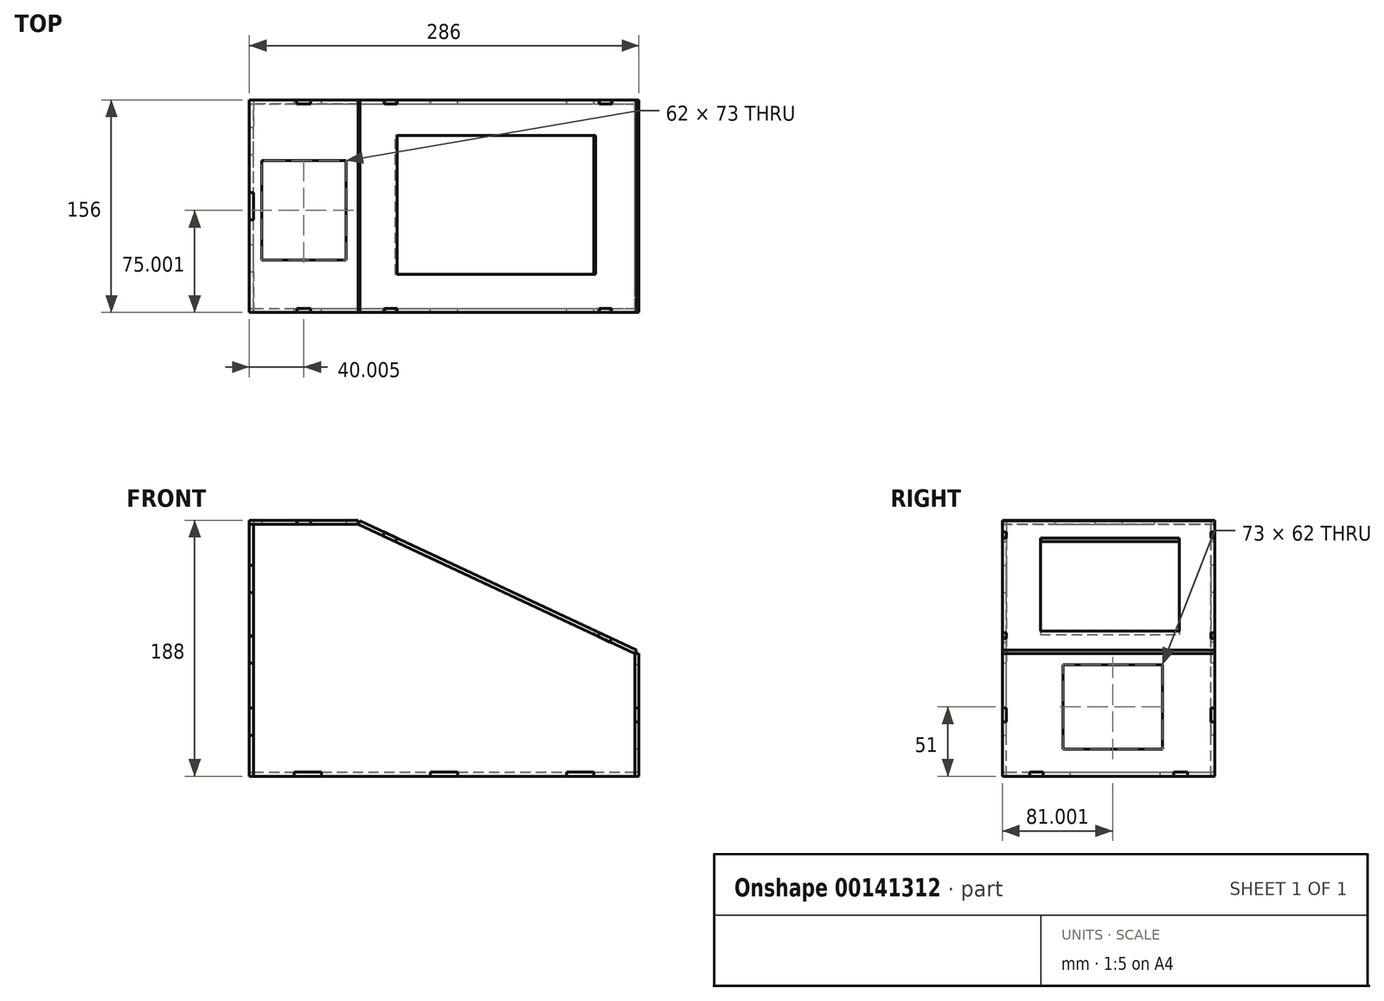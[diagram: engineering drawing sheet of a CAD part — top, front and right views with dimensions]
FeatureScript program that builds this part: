
annotation { "Feature Type Name" : "Feature", "Feature Type Description" : "" }
export const myFeature = defineFeature(function(context is Context, id is Id, definition is map)
    precondition{}
    {
        {
            var Q0;
            Q0=qCreatedBy(makeId("Top.planeOp"),FACE);
            var sketch = newSketch(context, id + "F0", { "sketchPlane" : qUnion([Q0])});
            skLineSegment(sketch, "E0.bottom", {"start": v(-139.67, -69.24) * mm, "end": v(140.33, -69.24) * mm});
            skLineSegment(sketch, "E0.top", {"start": v(-139.67, 80.76) * mm, "end": v(140.33, 80.76) * mm});
            skLineSegment(sketch, "E0.left", {"start": v(-139.67, -69.24) * mm, "end": v(-139.67, 80.76) * mm});
            skLineSegment(sketch, "E0.right", {"start": v(140.33, -69.24) * mm, "end": v(140.33, 80.76) * mm});
            skSolve(sketch);
        }
        {
            var Q0;
            Q0=makeQuery(id+"F0.imprint","IMPRINT",FACE,{"disambiguationData":[TD([[makeQuery(id+"F0.imprint","IMPRINT",EDGE,{"derivedFrom":sQuery(id+"F0.wireOp",EDGE,"E0.bottom")}),1.0]])]});
            extrude(context, id + "F1", {"entities" : qUnion([Q0]), "depth" : 3 * mm});
        }
        {
            var Q0;
            Q0=makeQuery(id+"F1.opExtrude","SWEPT_FACE",FACE,{"disambiguationData":[OSD([sQuery(id+"F0.wireOp",EDGE,"E0.right")])]});
            var sketch = newSketch(context, id + "F2", { "sketchPlane" : qUnion([Q0])});
            skLineSegment(sketch, "E1.bottom", {"start": v(-72.24, 0) * mm, "end": v(83.76, 0) * mm});
            skLineSegment(sketch, "E1.top", {"start": v(-72.24, 90) * mm, "end": v(83.76, 90) * mm});
            skLineSegment(sketch, "E1.left", {"start": v(-72.24, 0) * mm, "end": v(-72.24, 90) * mm});
            skLineSegment(sketch, "E1.right", {"start": v(83.76, 0) * mm, "end": v(83.76, 90) * mm});
            skLineSegment(sketch, "E2.bottom", {"start": v(-27.74, 82) * mm, "end": v(45.26, 82) * mm});
            skLineSegment(sketch, "E2.top", {"start": v(-27.74, 20) * mm, "end": v(45.26, 20) * mm});
            skLineSegment(sketch, "E2.left", {"start": v(-27.74, 82) * mm, "end": v(-27.74, 20) * mm});
            skLineSegment(sketch, "E2.right", {"start": v(45.26, 82) * mm, "end": v(45.26, 20) * mm});
            skLineSegment(sketch, "E3.bottom", {"start": v(-72.24, 50) * mm, "end": v(-69.24, 50) * mm});
            skLineSegment(sketch, "E3.top", {"start": v(-72.24, 40) * mm, "end": v(-69.24, 40) * mm});
            skLineSegment(sketch, "E3.left", {"start": v(-72.24, 50) * mm, "end": v(-72.24, 40) * mm});
            skLineSegment(sketch, "E3.right", {"start": v(-69.24, 50) * mm, "end": v(-69.24, 40) * mm});
            skLineSegment(sketch, "E4.bottom", {"start": v(83.76, 50) * mm, "end": v(80.76, 50) * mm});
            skLineSegment(sketch, "E4.top", {"start": v(83.76, 40) * mm, "end": v(80.76, 40) * mm});
            skLineSegment(sketch, "E4.left", {"start": v(83.76, 50) * mm, "end": v(83.76, 40) * mm});
            skLineSegment(sketch, "E4.right", {"start": v(80.76, 50) * mm, "end": v(80.76, 40) * mm});
            skLineSegment(sketch, "E5.bottom", {"start": v(-52.24, 0) * mm, "end": v(-42.24, 0) * mm});
            skLineSegment(sketch, "E5.top", {"start": v(-52.24, 3) * mm, "end": v(-42.24, 3) * mm});
            skLineSegment(sketch, "E5.left", {"start": v(-52.24, 0) * mm, "end": v(-52.24, 3) * mm});
            skLineSegment(sketch, "E5.right", {"start": v(-42.24, 0) * mm, "end": v(-42.24, 3) * mm});
            skLineSegment(sketch, "E6.bottom", {"start": v(63.76, 0) * mm, "end": v(53.76, 0) * mm});
            skLineSegment(sketch, "E6.top", {"start": v(63.76, 3) * mm, "end": v(53.76, 3) * mm});
            skLineSegment(sketch, "E6.left", {"start": v(63.76, 0) * mm, "end": v(63.76, 3) * mm});
            skLineSegment(sketch, "E6.right", {"start": v(53.76, 0) * mm, "end": v(53.76, 3) * mm});
            skSolve(sketch);
        }
        {
            var Q0;
            Q0=makeQuery(id+"F2.imprint","IMPRINT",FACE,{"disambiguationData":[TD([[makeQuery(id+"F2.imprint","IMPRINT",EDGE,{"derivedFrom":sQuery(id+"F2.wireOp",EDGE,"E1.top")}),-1.0]])]});
            var Q1;
            {var subQ1=sQuery(id+"F0.wireOp",EDGE,"E0.right");Q1=makeQuery(id+"F2.imprint","IMPRINT",FACE,{"disambiguationData":[TD([[makeQuery(id+"F2.imprint","IMPRINT",EDGE,{"derivedFrom":makeQuery(id+"F1.opExtrude","CAP_EDGE",EDGE,{"disambiguationData":[OSD([subQ1])],"isStart":false})}),-1.0]])]});}
            extrude(context, id + "F3", {"entities" : qUnion([Q0, Q1]), "depth" : 3 * mm});
        }
        {
            var Q0;
            Q0=makeQuery(id+"F1.opExtrude","SWEPT_FACE",FACE,{"disambiguationData":[OSD([sQuery(id+"F0.wireOp",EDGE,"E0.left")])]});
            var sketch = newSketch(context, id + "F4", { "sketchPlane" : qUnion([Q0])});
            skLineSegment(sketch, "E7.bottom", {"start": v(-83.76, 0) * mm, "end": v(72.24, 0) * mm});
            skLineSegment(sketch, "E7.top", {"start": v(-83.76, 185) * mm, "end": v(-15.76, 185) * mm});
            skLineSegment(sketch, "E7.left", {"start": v(-83.76, 0) * mm, "end": v(-83.76, 30) * mm});
            skLineSegment(sketch, "E7.right", {"start": v(72.24, 0) * mm, "end": v(72.24, 30) * mm});
            skLineSegment(sketch, "E8.bottom", {"start": v(72.24, 155) * mm, "end": v(69.24, 155) * mm});
            skLineSegment(sketch, "E8.top", {"start": v(72.24, 135) * mm, "end": v(69.24, 135) * mm});
            skLineSegment(sketch, "E8.right", {"start": v(69.24, 155) * mm, "end": v(69.24, 135) * mm});
            skPoint(sketch, "E9.oppositeSnap0", {"position": v(70.74, 135) * mm});
            skLineSegment(sketch, "E9.bottom", {"start": v(-83.76, 155) * mm, "end": v(-80.76, 155) * mm});
            skLineSegment(sketch, "E9.top", {"start": v(-83.76, 135) * mm, "end": v(-80.76, 135) * mm});
            skLineSegment(sketch, "E9.right", {"start": v(-80.76, 155) * mm, "end": v(-80.76, 135) * mm});
            skLineSegment(sketch, "E10.bottom", {"start": v(-83.76, 50) * mm, "end": v(-80.76, 50) * mm});
            skLineSegment(sketch, "E10.top", {"start": v(-83.76, 30) * mm, "end": v(-80.76, 30) * mm});
            skLineSegment(sketch, "E10.right", {"start": v(-80.76, 50) * mm, "end": v(-80.76, 30) * mm});
            skLineSegment(sketch, "E11.bottom", {"start": v(72.24, 30) * mm, "end": v(69.24, 30) * mm});
            skLineSegment(sketch, "E11.top", {"start": v(72.24, 50) * mm, "end": v(69.24, 50) * mm});
            skLineSegment(sketch, "E11.right", {"start": v(69.24, 30) * mm, "end": v(69.24, 50) * mm});
            skLineSegment(sketch, "E12.bottom", {"start": v(72.24, 103) * mm, "end": v(69.24, 103) * mm});
            skLineSegment(sketch, "E12.top", {"start": v(72.24, 83) * mm, "end": v(69.24, 83) * mm});
            skLineSegment(sketch, "E12.right", {"start": v(69.24, 103) * mm, "end": v(69.24, 83) * mm});
            skLineSegment(sketch, "E13.bottom", {"start": v(-83.76, 103) * mm, "end": v(-80.76, 103) * mm});
            skLineSegment(sketch, "E13.top", {"start": v(-83.76, 83) * mm, "end": v(-80.76, 83) * mm});
            skLineSegment(sketch, "E13.right", {"start": v(-80.76, 103) * mm, "end": v(-80.76, 83) * mm});
            skLineSegment(sketch, "E14.trimOffspring", {"start": v(72.24, 50) * mm, "end": v(72.24, 83) * mm});
            skLineSegment(sketch, "E15.trimOffspring", {"start": v(72.24, 103) * mm, "end": v(72.24, 135) * mm});
            skLineSegment(sketch, "E16.trimOffspring", {"start": v(72.24, 155) * mm, "end": v(72.24, 185) * mm});
            skLineSegment(sketch, "E17.trimOffspring", {"start": v(-83.76, 50) * mm, "end": v(-83.76, 83) * mm});
            skLineSegment(sketch, "E18.trimOffspring", {"start": v(-83.76, 103) * mm, "end": v(-83.76, 135) * mm});
            skLineSegment(sketch, "E19.trimOffspring", {"start": v(-83.76, 155) * mm, "end": v(-83.76, 185) * mm});
            skLineSegment(sketch, "E20.trimOffspring", {"start": v(4.24, 185) * mm, "end": v(72.24, 185) * mm});
            skLineSegment(sketch, "E21.bottom", {"start": v(42.24, 0) * mm, "end": v(22.24, 0) * mm});
            skLineSegment(sketch, "E21.top", {"start": v(42.24, 3) * mm, "end": v(22.24, 3) * mm});
            skLineSegment(sketch, "E21.left", {"start": v(42.24, 0) * mm, "end": v(42.24, 3) * mm});
            skLineSegment(sketch, "E21.right", {"start": v(22.24, 0) * mm, "end": v(22.24, 3) * mm});
            skLineSegment(sketch, "E22.bottom", {"start": v(-63.76, 0) * mm, "end": v(-43.76, 0) * mm});
            skLineSegment(sketch, "E22.top", {"start": v(-63.76, 3) * mm, "end": v(-43.76, 3) * mm});
            skLineSegment(sketch, "E22.left", {"start": v(-43.76, 0) * mm, "end": v(-43.76, 3) * mm});
            skLineSegment(sketch, "E22.right", {"start": v(-63.76, 0) * mm, "end": v(-63.76, 3) * mm});
            skLineSegment(sketch, "E23.bottom", {"start": v(-15.76, 185) * mm, "end": v(4.24, 185) * mm});
            skLineSegment(sketch, "E23.top", {"start": v(-15.76, 188) * mm, "end": v(4.24, 188) * mm});
            skLineSegment(sketch, "E23.left", {"start": v(-15.76, 185) * mm, "end": v(-15.76, 188) * mm});
            skLineSegment(sketch, "E23.right", {"start": v(4.24, 185) * mm, "end": v(4.24, 188) * mm});
            skSolve(sketch);
        }
        {
            var Q0;
            Q0=makeQuery(id+"F4.imprint","IMPRINT",FACE,{"disambiguationData":[TD([[makeQuery(id+"F4.imprint","IMPRINT",EDGE,{"derivedFrom":sQuery(id+"F4.wireOp",EDGE,"E7.top")}),-1.0]])]});
            var Q1;
            {var subQ1=sQuery(id+"F0.wireOp",EDGE,"E0.left");Q1=makeQuery(id+"F4.imprint","IMPRINT",FACE,{"disambiguationData":[TD([[makeQuery(id+"F4.imprint","IMPRINT",EDGE,{"derivedFrom":makeQuery(id+"F1.opExtrude","CAP_EDGE",EDGE,{"disambiguationData":[OSD([subQ1])],"isStart":false})}),1.0]])]});}
            extrude(context, id + "F5", {"entities" : qUnion([Q0, Q1]), "depth" : 3 * mm});
        }
        {
            var Q0;
            Q0=makeQuery(id+"F5.opExtrude","SWEPT_FACE",FACE,{"disambiguationData":[OSD([sQuery(id+"F4.wireOp",EDGE,"E7.top")])]});
            var sketch = newSketch(context, id + "F6", { "sketchPlane" : qUnion([Q0])});
            skLineSegment(sketch, "E24.bottom", {"start": v(-142.67, -72.24) * mm, "end": v(-62.67, -72.24) * mm});
            skLineSegment(sketch, "E24.top", {"start": v(-142.67, 83.76) * mm, "end": v(-62.67, 83.76) * mm});
            skLineSegment(sketch, "E24.left", {"start": v(-142.67, -72.24) * mm, "end": v(-142.67, 83.76) * mm});
            skLineSegment(sketch, "E24.right", {"start": v(-62.67, -72.24) * mm, "end": v(-62.67, 83.76) * mm});
            skLineSegment(sketch, "E25.bottom", {"start": v(-133.67, -33.74) * mm, "end": v(-71.67, -33.74) * mm});
            skLineSegment(sketch, "E25.top", {"start": v(-133.67, 39.26) * mm, "end": v(-71.67, 39.26) * mm});
            skLineSegment(sketch, "E25.left", {"start": v(-133.67, -33.74) * mm, "end": v(-133.67, 39.26) * mm});
            skLineSegment(sketch, "E25.right", {"start": v(-71.67, -33.74) * mm, "end": v(-71.67, 39.26) * mm});
            skLineSegment(sketch, "E26.bottom", {"start": v(-142.67, 15.76) * mm, "end": v(-139.67, 15.76) * mm});
            skLineSegment(sketch, "E26.top", {"start": v(-142.67, -4.24) * mm, "end": v(-139.67, -4.24) * mm});
            skLineSegment(sketch, "E26.left", {"start": v(-142.67, 15.76) * mm, "end": v(-142.67, -4.24) * mm});
            skLineSegment(sketch, "E26.right", {"start": v(-139.67, 15.76) * mm, "end": v(-139.67, -4.24) * mm});
            skLineSegment(sketch, "E27.bottom", {"start": v(-97.67, 83.76) * mm, "end": v(-107.67, 83.76) * mm});
            skLineSegment(sketch, "E27.top", {"start": v(-97.67, 80.76) * mm, "end": v(-107.67, 80.76) * mm});
            skLineSegment(sketch, "E27.left", {"start": v(-97.67, 83.76) * mm, "end": v(-97.67, 80.76) * mm});
            skLineSegment(sketch, "E27.right", {"start": v(-107.67, 83.76) * mm, "end": v(-107.67, 80.76) * mm});
            skLineSegment(sketch, "E28.bottom", {"start": v(-97.67, -72.24) * mm, "end": v(-107.67, -72.24) * mm});
            skLineSegment(sketch, "E28.top", {"start": v(-97.67, -69.24) * mm, "end": v(-107.67, -69.24) * mm});
            skLineSegment(sketch, "E28.left", {"start": v(-97.67, -72.24) * mm, "end": v(-97.67, -69.24) * mm});
            skLineSegment(sketch, "E28.right", {"start": v(-107.67, -72.24) * mm, "end": v(-107.67, -69.24) * mm});
            skSolve(sketch);
        }
        {
            var Q0;
            {var subQ0=sQuery(id+"F6.wireOp",EDGE,"E24.left");Q0=makeQuery(id+"F6.imprint","IMPRINT",FACE,{"disambiguationData":[TD([[makeQuery(id+"F6.imprint","IMPRINT",EDGE,{"derivedFrom":subQ0}),1.0]])]});}
            var Q1;
            {var subQ0=sQuery(id+"F6.wireOp",EDGE,"E24.right");Q1=makeQuery(id+"F6.imprint","IMPRINT",FACE,{"disambiguationData":[TD([[makeQuery(id+"F6.imprint","IMPRINT",EDGE,{"derivedFrom":subQ0}),1.0]])]});}
            extrude(context, id + "F7", {"entities" : qUnion([Q0, Q1]), "depth" : 3 * mm});
        }
        {
            var Q0;
            Q0=makeQuery(id+"F1.opExtrude","SWEPT_FACE",FACE,{"disambiguationData":[OSD([sQuery(id+"F0.wireOp",EDGE,"E0.bottom")])]});
            var sketch = newSketch(context, id + "F8", { "sketchPlane" : qUnion([Q0])});
            skLineSegment(sketch, "E29.bottom", {"start": v(-139.67, 0) * mm, "end": v(140.33, 0) * mm});
            skLineSegment(sketch, "E29.top", {"start": v(-139.67, 185) * mm, "end": v(-62.67, 185) * mm});
            skLineSegment(sketch, "E29.left", {"start": v(-139.67, 0) * mm, "end": v(-139.67, 185) * mm});
            skLineSegment(sketch, "E29.right", {"start": v(140.33, 0) * mm, "end": v(140.33, 90) * mm});
            skLineSegment(sketch, "E30", {"start": v(-62.67, 185) * mm, "end": v(140.33, 90) * mm});
            skPoint(sketch, "E31.orphan", {"position": v(140.33, 185) * mm});
            skSolve(sketch);
        }
        {
            var Q0;
            {var subQ4=sQuery(id+"F8.wireOp",EDGE,"E29.top");Q0=makeQuery(id+"F8.imprint","IMPRINT",FACE,{"disambiguationData":[TD([[makeQuery(id+"F8.imprint","IMPRINT",EDGE,{"derivedFrom":subQ4}),-1.0]])]});}
            var Q1;
            {var subQ0=sQuery(id+"F8.wireOp",EDGE,"E29.bottom");Q1=makeQuery(id+"F8.imprint","IMPRINT",FACE,{"disambiguationData":[TD([[makeQuery(id+"F8.imprint","IMPRINT",EDGE,{"derivedFrom":subQ0}),1.0]])]});}
            extrude(context, id + "F9", {"entities" : qUnion([Q0, Q1]), "depth" : 3 * mm});
        }
        {
            var Q0;
            Q0=makeQuery(id+"F1.opExtrude","SWEPT_FACE",FACE,{"disambiguationData":[OSD([sQuery(id+"F0.wireOp",EDGE,"E0.top")])]});
            var sketch = newSketch(context, id + "F10", { "sketchPlane" : qUnion([Q0])});
            skLineSegment(sketch, "E32.bottom", {"start": v(-140.33, 0) * mm, "end": v(139.67, 0) * mm});
            skLineSegment(sketch, "E32.top", {"start": v(62.67, 185) * mm, "end": v(139.67, 185) * mm});
            skLineSegment(sketch, "E32.left", {"start": v(-140.33, 0) * mm, "end": v(-140.33, 90) * mm});
            skLineSegment(sketch, "E32.right", {"start": v(139.67, 0) * mm, "end": v(139.67, 185) * mm});
            skLineSegment(sketch, "E33", {"start": v(62.67, 185) * mm, "end": v(-140.33, 90) * mm});
            skSolve(sketch);
        }
        {
            var Q0;
            {var subQ3=sQuery(id+"F10.wireOp",EDGE,"E32.top");Q0=makeQuery(id+"F10.imprint","IMPRINT",FACE,{"disambiguationData":[TD([[makeQuery(id+"F10.imprint","IMPRINT",EDGE,{"derivedFrom":subQ3}),-1.0]])]});}
            var Q1;
            {var subQ0=sQuery(id+"F10.wireOp",EDGE,"E32.bottom");Q1=makeQuery(id+"F10.imprint","IMPRINT",FACE,{"disambiguationData":[TD([[makeQuery(id+"F10.imprint","IMPRINT",EDGE,{"derivedFrom":subQ0}),-1.0]])]});}
            extrude(context, id + "F11", {"entities" : qUnion([Q0, Q1]), "depth" : 3 * mm});
        }
        {
            var Q0;
            Q0=makeQuery(id+"F9.opExtrude","SWEPT_FACE",FACE,{"disambiguationData":[OSD([sQuery(id+"F8.wireOp",EDGE,"E30")])]});
            var sketch = newSketch(context, id + "F12", { "sketchPlane" : qUnion([Q0])});
            skLineSegment(sketch, "E34.bottom", {"start": v(88.96, -72.24) * mm, "end": v(-135.1, -72.24) * mm});
            skLineSegment(sketch, "E34.top", {"start": v(88.96, 83.76) * mm, "end": v(-135.1, 83.76) * mm});
            skLineSegment(sketch, "E34.left", {"start": v(88.96, -72.24) * mm, "end": v(88.96, 83.76) * mm});
            skLineSegment(sketch, "E34.right", {"start": v(-135.1, -72.24) * mm, "end": v(-135.1, 83.76) * mm});
            skLineSegment(sketch, "E35.bottom", {"start": v(-105.1, -44.24) * mm, "end": v(55.9, -44.24) * mm});
            skLineSegment(sketch, "E35.top", {"start": v(-105.1, 57.76) * mm, "end": v(55.9, 57.76) * mm});
            skLineSegment(sketch, "E35.left", {"start": v(-105.1, -44.24) * mm, "end": v(-105.1, 57.76) * mm});
            skLineSegment(sketch, "E35.right", {"start": v(55.9, -44.24) * mm, "end": v(55.9, 57.76) * mm});
            skLineSegment(sketch, "E36.bottom", {"start": v(-115.1, 83.76) * mm, "end": v(-105.1, 83.76) * mm});
            skLineSegment(sketch, "E36.top", {"start": v(-115.1, 80.76) * mm, "end": v(-105.1, 80.76) * mm});
            skLineSegment(sketch, "E36.left", {"start": v(-115.1, 83.76) * mm, "end": v(-115.1, 80.76) * mm});
            skLineSegment(sketch, "E36.right", {"start": v(-105.1, 83.76) * mm, "end": v(-105.1, 80.76) * mm});
            skLineSegment(sketch, "E37.bottom", {"start": v(-115.1, -72.24) * mm, "end": v(-105.1, -72.24) * mm});
            skLineSegment(sketch, "E37.top", {"start": v(-115.1, -69.24) * mm, "end": v(-105.1, -69.24) * mm});
            skLineSegment(sketch, "E37.left", {"start": v(-115.1, -72.24) * mm, "end": v(-115.1, -69.24) * mm});
            skLineSegment(sketch, "E37.right", {"start": v(-105.1, -72.24) * mm, "end": v(-105.1, -69.24) * mm});
            skLineSegment(sketch, "E38.bottom", {"start": v(58.96, -69.24) * mm, "end": v(68.96, -69.24) * mm});
            skLineSegment(sketch, "E38.top", {"start": v(58.96, -72.24) * mm, "end": v(68.96, -72.24) * mm});
            skLineSegment(sketch, "E38.left", {"start": v(58.96, -69.24) * mm, "end": v(58.96, -72.24) * mm});
            skLineSegment(sketch, "E38.right", {"start": v(68.96, -69.24) * mm, "end": v(68.96, -72.24) * mm});
            skLineSegment(sketch, "E39.bottom", {"start": v(68.96, 83.76) * mm, "end": v(58.96, 83.76) * mm});
            skLineSegment(sketch, "E39.top", {"start": v(68.96, 80.76) * mm, "end": v(58.96, 80.76) * mm});
            skLineSegment(sketch, "E39.left", {"start": v(68.96, 83.76) * mm, "end": v(68.96, 80.76) * mm});
            skLineSegment(sketch, "E39.right", {"start": v(58.96, 83.76) * mm, "end": v(58.96, 80.76) * mm});
            skSolve(sketch);
        }
        {
            var Q0;
            {var subQ0=sQuery(id+"F12.wireOp",EDGE,"E34.bottom");Q0=makeQuery(id+"F12.imprint","IMPRINT",FACE,{"disambiguationData":[TD([[makeQuery(id+"F12.imprint","IMPRINT",EDGE,{"derivedFrom":subQ0}),1.0]])]});}
            var Q1;
            {var subQ0=sQuery(id+"F12.wireOp",EDGE,"E34.top");Q1=makeQuery(id+"F12.imprint","IMPRINT",FACE,{"disambiguationData":[TD([[makeQuery(id+"F12.imprint","IMPRINT",EDGE,{"derivedFrom":subQ0}),1.0]])]});}
            extrude(context, id + "F13", {"entities" : qUnion([Q0, Q1]), "depth" : 3 * mm});
        }
        {
            var Q0;
            Q0=makeQuery(id+"F5.opExtrude","SWEPT_FACE",FACE,{"disambiguationData":[OSD([sQuery(id+"F4.wireOp",EDGE,"E7.top"),sQuery(id+"F4.wireOp",EDGE,"E20.trimOffspring"),sQuery(id+"F4.wireOp",EDGE,"E23.bottom")])]});
            var sketch = newSketch(context, id + "F14", { "sketchPlane" : qUnion([Q0])});
            skLineSegment(sketch, "E40.bottom", {"start": v(-142.67, 15.75) * mm, "end": v(-139.67, 15.75) * mm});
            skLineSegment(sketch, "E40.top", {"start": v(-142.67, -4.22) * mm, "end": v(-139.67, -4.22) * mm});
            skLineSegment(sketch, "E40.left", {"start": v(-142.67, 15.75) * mm, "end": v(-142.67, -4.22) * mm});
            skLineSegment(sketch, "E40.right", {"start": v(-139.67, 15.75) * mm, "end": v(-139.67, -4.22) * mm});
            skSolve(sketch);
        }
        {
            var Q0;
            Q0=makeQuery(id+"F14.imprint","IMPRINT",FACE,{"disambiguationData":[TD([[makeQuery(id+"F14.imprint","IMPRINT",EDGE,{"derivedFrom":sQuery(id+"F14.wireOp",EDGE,"E40.bottom")}),-1.0]])]});
            extrude(context, id + "F15", {"entities" : qUnion([Q0]), "depth" : 3 * mm});
        }
        {
            var Q0;
            Q0=makeQuery(id+"F9.opExtrude","SWEPT_FACE",FACE,{"disambiguationData":[OSD([sQuery(id+"F8.wireOp",EDGE,"E29.left")])]});
            var sketch = newSketch(context, id + "F16", { "sketchPlane" : qUnion([Q0])});
            skLineSegment(sketch, "E41.bottom", {"start": v(72.24, 135) * mm, "end": v(69.24, 135) * mm});
            skLineSegment(sketch, "E41.top", {"start": v(72.24, 154.98) * mm, "end": v(69.24, 154.98) * mm});
            skLineSegment(sketch, "E41.left", {"start": v(72.24, 135) * mm, "end": v(72.24, 154.98) * mm});
            skLineSegment(sketch, "E41.right", {"start": v(69.24, 135) * mm, "end": v(69.24, 154.98) * mm});
            skLineSegment(sketch, "E42.bottom", {"start": v(72.24, 83) * mm, "end": v(69.24, 83) * mm});
            skLineSegment(sketch, "E42.top", {"start": v(72.24, 102.97) * mm, "end": v(69.24, 102.97) * mm});
            skLineSegment(sketch, "E42.left", {"start": v(72.24, 83) * mm, "end": v(72.24, 102.97) * mm});
            skLineSegment(sketch, "E42.right", {"start": v(69.24, 83) * mm, "end": v(69.24, 102.97) * mm});
            skLineSegment(sketch, "E43.bottom", {"start": v(72.24, 30) * mm, "end": v(69.24, 30) * mm});
            skLineSegment(sketch, "E43.top", {"start": v(72.24, 49.98) * mm, "end": v(69.24, 49.98) * mm});
            skLineSegment(sketch, "E43.left", {"start": v(72.24, 30) * mm, "end": v(72.24, 49.98) * mm});
            skLineSegment(sketch, "E43.right", {"start": v(69.24, 30) * mm, "end": v(69.24, 49.98) * mm});
            skSolve(sketch);
        }
        {
            var Q0;
            Q0=makeQuery(id+"F16.imprint","IMPRINT",FACE,{"disambiguationData":[TD([[makeQuery(id+"F16.imprint","IMPRINT",EDGE,{"derivedFrom":sQuery(id+"F16.wireOp",EDGE,"E41.bottom")}),-1.0]])]});
            var Q1;
            Q1=makeQuery(id+"F16.imprint","IMPRINT",FACE,{"disambiguationData":[TD([[makeQuery(id+"F16.imprint","IMPRINT",EDGE,{"derivedFrom":sQuery(id+"F16.wireOp",EDGE,"E42.bottom")}),-1.0]])]});
            var Q2;
            Q2=makeQuery(id+"F16.imprint","IMPRINT",FACE,{"disambiguationData":[TD([[makeQuery(id+"F16.imprint","IMPRINT",EDGE,{"derivedFrom":sQuery(id+"F16.wireOp",EDGE,"E43.bottom")}),-1.0]])]});
            extrude(context, id + "F17", {"entities" : qUnion([Q0, Q1, Q2]), "depth" : 3 * mm});
        }
        {
            var Q0;
            Q0=makeQuery(id+"F1.opExtrude","SWEPT_FACE",FACE,{"disambiguationData":[OSD([sQuery(id+"F0.wireOp",EDGE,"E0.left")])]});
            var sketch = newSketch(context, id + "F18", { "sketchPlane" : qUnion([Q0])});
            skLineSegment(sketch, "E44.bottom", {"start": v(42.23, 0) * mm, "end": v(22.26, 0) * mm});
            skLineSegment(sketch, "E44.top", {"start": v(42.23, 3) * mm, "end": v(22.26, 3) * mm});
            skLineSegment(sketch, "E44.left", {"start": v(42.23, 0) * mm, "end": v(42.23, 3) * mm});
            skLineSegment(sketch, "E44.right", {"start": v(22.26, 0) * mm, "end": v(22.26, 3) * mm});
            skLineSegment(sketch, "E45.bottom", {"start": v(-43.78, 0) * mm, "end": v(-63.73, 0) * mm});
            skLineSegment(sketch, "E45.top", {"start": v(-43.78, 3) * mm, "end": v(-63.73, 3) * mm});
            skLineSegment(sketch, "E45.left", {"start": v(-43.78, 0) * mm, "end": v(-43.78, 3) * mm});
            skLineSegment(sketch, "E45.right", {"start": v(-63.73, 0) * mm, "end": v(-63.73, 3) * mm});
            skSolve(sketch);
        }
        {
            var Q0;
            Q0=makeQuery(id+"F18.imprint","IMPRINT",FACE,{"disambiguationData":[TD([[makeQuery(id+"F18.imprint","IMPRINT",EDGE,{"derivedFrom":sQuery(id+"F18.wireOp",EDGE,"E45.bottom")}),-1.0]])]});
            var Q1;
            Q1=makeQuery(id+"F18.imprint","IMPRINT",FACE,{"disambiguationData":[TD([[makeQuery(id+"F18.imprint","IMPRINT",EDGE,{"derivedFrom":sQuery(id+"F18.wireOp",EDGE,"E44.bottom")}),-1.0]])]});
            extrude(context, id + "F19", {"entities" : qUnion([Q0, Q1]), "depth" : 3 * mm});
        }
        {
            var Q0;
            Q0=makeQuery(id+"F11.opExtrude","SWEPT_FACE",FACE,{"disambiguationData":[OSD([sQuery(id+"F10.wireOp",EDGE,"E32.right")])]});
            var sketch = newSketch(context, id + "F20", { "sketchPlane" : qUnion([Q0])});
            skLineSegment(sketch, "E46.bottom", {"start": v(-83.76, 155) * mm, "end": v(-80.76, 155) * mm});
            skLineSegment(sketch, "E46.top", {"start": v(-83.76, 135.02) * mm, "end": v(-80.76, 135.02) * mm});
            skLineSegment(sketch, "E46.left", {"start": v(-83.76, 155) * mm, "end": v(-83.76, 135.02) * mm});
            skLineSegment(sketch, "E46.right", {"start": v(-80.76, 155) * mm, "end": v(-80.76, 135.02) * mm});
            skLineSegment(sketch, "E47.bottom", {"start": v(-83.76, 83) * mm, "end": v(-80.76, 83) * mm});
            skLineSegment(sketch, "E47.top", {"start": v(-83.76, 102.98) * mm, "end": v(-80.76, 102.98) * mm});
            skLineSegment(sketch, "E47.left", {"start": v(-83.76, 83) * mm, "end": v(-83.76, 102.98) * mm});
            skLineSegment(sketch, "E47.right", {"start": v(-80.76, 83) * mm, "end": v(-80.76, 102.98) * mm});
            skLineSegment(sketch, "E48.bottom", {"start": v(-83.76, 50) * mm, "end": v(-80.76, 50) * mm});
            skLineSegment(sketch, "E48.top", {"start": v(-83.76, 30.01) * mm, "end": v(-80.76, 30.01) * mm});
            skLineSegment(sketch, "E48.left", {"start": v(-83.76, 50) * mm, "end": v(-83.76, 30.01) * mm});
            skLineSegment(sketch, "E48.right", {"start": v(-80.76, 50) * mm, "end": v(-80.76, 30.01) * mm});
            skSolve(sketch);
        }
        {
            var Q0;
            Q0=makeQuery(id+"F20.imprint","IMPRINT",FACE,{"disambiguationData":[TD([[makeQuery(id+"F20.imprint","IMPRINT",EDGE,{"derivedFrom":sQuery(id+"F20.wireOp",EDGE,"E46.bottom")}),-1.0]])]});
            var Q1;
            Q1=makeQuery(id+"F20.imprint","IMPRINT",FACE,{"disambiguationData":[TD([[makeQuery(id+"F20.imprint","IMPRINT",EDGE,{"derivedFrom":sQuery(id+"F20.wireOp",EDGE,"E47.bottom")}),1.0]])]});
            var Q2;
            Q2=makeQuery(id+"F20.imprint","IMPRINT",FACE,{"disambiguationData":[TD([[makeQuery(id+"F20.imprint","IMPRINT",EDGE,{"derivedFrom":sQuery(id+"F20.wireOp",EDGE,"E48.bottom")}),-1.0]])]});
            extrude(context, id + "F21", {"entities" : qUnion([Q0, Q1, Q2]), "depth" : 3 * mm});
        }
        {
            var Q0;
            Q0=makeQuery(id+"F11.opExtrude","SWEPT_BODY",BODY,{"disambiguationData":[OSD([sQuery(id+"F10.wireOp",EDGE,"E32.bottom"),sQuery(id+"F10.wireOp",EDGE,"E32.top"),sQuery(id+"F10.wireOp",EDGE,"E32.left"),sQuery(id+"F10.wireOp",EDGE,"E32.right"),sQuery(id+"F10.wireOp",EDGE,"E33")])]});
            var Q1;
            Q1=makeQuery(id+"F21.opExtrude","SWEPT_BODY",BODY,{"disambiguationData":[OSD([sQuery(id+"F20.wireOp",EDGE,"E48.bottom"),sQuery(id+"F20.wireOp",EDGE,"E48.top"),sQuery(id+"F20.wireOp",EDGE,"E48.left"),sQuery(id+"F20.wireOp",EDGE,"E48.right")])]});
            var Q2;
            Q2=makeQuery(id+"F21.opExtrude","SWEPT_BODY",BODY,{"disambiguationData":[OSD([sQuery(id+"F20.wireOp",EDGE,"E47.bottom"),sQuery(id+"F20.wireOp",EDGE,"E47.top"),sQuery(id+"F20.wireOp",EDGE,"E47.left"),sQuery(id+"F20.wireOp",EDGE,"E47.right")])]});
            var Q3;
            Q3=makeQuery(id+"F21.opExtrude","SWEPT_BODY",BODY,{"disambiguationData":[OSD([sQuery(id+"F20.wireOp",EDGE,"E46.bottom"),sQuery(id+"F20.wireOp",EDGE,"E46.top"),sQuery(id+"F20.wireOp",EDGE,"E46.left"),sQuery(id+"F20.wireOp",EDGE,"E46.right")])]});
            booleanBodies(context, id + "F22", {"operationType" : BooleanOperationType.UNION, "tools" : qUnion([Q0, Q1, Q2, Q3])});
        }
        {
            var Q0;
            Q0=makeQuery(id+"F11.opExtrude","SWEPT_FACE",FACE,{"disambiguationData":[OSD([sQuery(id+"F10.wireOp",EDGE,"E32.top")])]});
            var sketch = newSketch(context, id + "F23", { "sketchPlane" : qUnion([Q0])});
            skLineSegment(sketch, "E49.bottom", {"start": v(-107.66, 83.76) * mm, "end": v(-97.68, 83.76) * mm});
            skLineSegment(sketch, "E49.top", {"start": v(-107.66, 80.76) * mm, "end": v(-97.68, 80.76) * mm});
            skLineSegment(sketch, "E49.left", {"start": v(-107.66, 83.76) * mm, "end": v(-107.66, 80.76) * mm});
            skLineSegment(sketch, "E49.right", {"start": v(-97.68, 83.76) * mm, "end": v(-97.68, 80.76) * mm});
            skSolve(sketch);
        }
        {
            var Q0;
            Q0=makeQuery(id+"F23.imprint","IMPRINT",FACE,{"disambiguationData":[TD([[makeQuery(id+"F23.imprint","IMPRINT",EDGE,{"derivedFrom":sQuery(id+"F23.wireOp",EDGE,"E49.bottom")}),1.0]])]});
            extrude(context, id + "F24", {"entities" : qUnion([Q0]), "depth" : 3 * mm});
        }
        {
            var Q0;
            Q0=makeQuery(id+"F9.opExtrude","SWEPT_FACE",FACE,{"disambiguationData":[OSD([sQuery(id+"F8.wireOp",EDGE,"E29.top")])]});
            var sketch = newSketch(context, id + "F25", { "sketchPlane" : qUnion([Q0])});
            skLineSegment(sketch, "E50.bottom", {"start": v(-107.65, -72.24) * mm, "end": v(-97.67, -72.24) * mm});
            skLineSegment(sketch, "E50.top", {"start": v(-107.65, -69.24) * mm, "end": v(-97.67, -69.24) * mm});
            skLineSegment(sketch, "E50.left", {"start": v(-107.65, -72.24) * mm, "end": v(-107.65, -69.24) * mm});
            skLineSegment(sketch, "E50.right", {"start": v(-97.67, -72.24) * mm, "end": v(-97.67, -69.24) * mm});
            skSolve(sketch);
        }
        {
            var Q0;
            Q0=makeQuery(id+"F25.imprint","IMPRINT",FACE,{"disambiguationData":[TD([[makeQuery(id+"F25.imprint","IMPRINT",EDGE,{"derivedFrom":sQuery(id+"F25.wireOp",EDGE,"E50.bottom")}),1.0]])]});
            extrude(context, id + "F26", {"entities" : qUnion([Q0]), "depth" : 3 * mm});
        }
        {
            var Q0;
            Q0=makeQuery(id+"F11.opExtrude","SWEPT_FACE",FACE,{"disambiguationData":[OSD([sQuery(id+"F10.wireOp",EDGE,"E32.bottom")])]});
            var sketch = newSketch(context, id + "F27", { "sketchPlane" : qUnion([Q0])});
            skLineSegment(sketch, "E51.bottom", {"start": v(110.33, -80.76) * mm, "end": v(90.33, -80.76) * mm});
            skLineSegment(sketch, "E51.top", {"start": v(110.33, -83.76) * mm, "end": v(90.33, -83.76) * mm});
            skLineSegment(sketch, "E51.left", {"start": v(110.33, -80.76) * mm, "end": v(110.33, -83.76) * mm});
            skLineSegment(sketch, "E51.right", {"start": v(90.33, -80.76) * mm, "end": v(90.33, -83.76) * mm});
            skLineSegment(sketch, "E52.bottom", {"start": v(-109.67, -80.76) * mm, "end": v(-89.67, -80.76) * mm});
            skLineSegment(sketch, "E52.top", {"start": v(-109.67, -83.76) * mm, "end": v(-89.67, -83.76) * mm});
            skLineSegment(sketch, "E52.left", {"start": v(-109.67, -80.76) * mm, "end": v(-109.67, -83.76) * mm});
            skLineSegment(sketch, "E52.right", {"start": v(-89.67, -80.76) * mm, "end": v(-89.67, -83.76) * mm});
            skLineSegment(sketch, "E53.bottom", {"start": v(-9.67, -80.76) * mm, "end": v(10.33, -80.76) * mm});
            skLineSegment(sketch, "E53.top", {"start": v(-9.67, -83.76) * mm, "end": v(10.33, -83.76) * mm});
            skLineSegment(sketch, "E53.left", {"start": v(-9.67, -80.76) * mm, "end": v(-9.67, -83.76) * mm});
            skLineSegment(sketch, "E53.right", {"start": v(10.33, -80.76) * mm, "end": v(10.33, -83.76) * mm});
            skSolve(sketch);
        }
        {
            var Q0;
            Q0=makeQuery(id+"F27.imprint","IMPRINT",FACE,{"disambiguationData":[TD([[makeQuery(id+"F27.imprint","IMPRINT",EDGE,{"derivedFrom":sQuery(id+"F27.wireOp",EDGE,"E52.bottom")}),-1.0]])]});
            var Q1;
            Q1=makeQuery(id+"F27.imprint","IMPRINT",FACE,{"disambiguationData":[TD([[makeQuery(id+"F27.imprint","IMPRINT",EDGE,{"derivedFrom":sQuery(id+"F27.wireOp",EDGE,"E53.bottom")}),-1.0]])]});
            var Q2;
            Q2=makeQuery(id+"F27.imprint","IMPRINT",FACE,{"disambiguationData":[TD([[makeQuery(id+"F27.imprint","IMPRINT",EDGE,{"derivedFrom":sQuery(id+"F27.wireOp",EDGE,"E51.bottom")}),-1.0]])]});
            extrude(context, id + "F28", {"entities" : qUnion([Q0, Q1, Q2]), "operationType" : NewBodyOperationType.REMOVE, "oppositeDirection" : true, "depth" : 3 * mm});
        }
        {
            var Q0;
            Q0=makeQuery(id+"F9.opExtrude","SWEPT_FACE",FACE,{"disambiguationData":[OSD([sQuery(id+"F8.wireOp",EDGE,"E29.bottom")])]});
            var sketch = newSketch(context, id + "F29", { "sketchPlane" : qUnion([Q0])});
            skLineSegment(sketch, "E54.bottom", {"start": v(-109.67, 72.24) * mm, "end": v(-89.67, 72.24) * mm});
            skLineSegment(sketch, "E54.top", {"start": v(-109.67, 69.24) * mm, "end": v(-89.67, 69.24) * mm});
            skLineSegment(sketch, "E54.left", {"start": v(-109.67, 72.24) * mm, "end": v(-109.67, 69.24) * mm});
            skLineSegment(sketch, "E54.right", {"start": v(-89.67, 72.24) * mm, "end": v(-89.67, 69.24) * mm});
            skLineSegment(sketch, "E55.bottom", {"start": v(-9.67, 72.24) * mm, "end": v(10.33, 72.24) * mm});
            skLineSegment(sketch, "E55.top", {"start": v(-9.67, 69.24) * mm, "end": v(10.33, 69.24) * mm});
            skLineSegment(sketch, "E55.left", {"start": v(-9.67, 72.24) * mm, "end": v(-9.67, 69.24) * mm});
            skLineSegment(sketch, "E55.right", {"start": v(10.33, 72.24) * mm, "end": v(10.33, 69.24) * mm});
            skLineSegment(sketch, "E56.bottom", {"start": v(90.33, 72.24) * mm, "end": v(110.33, 72.24) * mm});
            skLineSegment(sketch, "E56.top", {"start": v(90.33, 69.24) * mm, "end": v(110.33, 69.24) * mm});
            skLineSegment(sketch, "E56.left", {"start": v(90.33, 72.24) * mm, "end": v(90.33, 69.24) * mm});
            skLineSegment(sketch, "E56.right", {"start": v(110.33, 72.24) * mm, "end": v(110.33, 69.24) * mm});
            skSolve(sketch);
        }
        {
            var Q0;
            Q0=makeQuery(id+"F29.imprint","IMPRINT",FACE,{"disambiguationData":[TD([[makeQuery(id+"F29.imprint","IMPRINT",EDGE,{"derivedFrom":sQuery(id+"F29.wireOp",EDGE,"E56.bottom")}),-1.0]])]});
            var Q1;
            Q1=makeQuery(id+"F29.imprint","IMPRINT",FACE,{"disambiguationData":[TD([[makeQuery(id+"F29.imprint","IMPRINT",EDGE,{"derivedFrom":sQuery(id+"F29.wireOp",EDGE,"E55.bottom")}),-1.0]])]});
            var Q2;
            Q2=makeQuery(id+"F29.imprint","IMPRINT",FACE,{"disambiguationData":[TD([[makeQuery(id+"F29.imprint","IMPRINT",EDGE,{"derivedFrom":sQuery(id+"F29.wireOp",EDGE,"E54.bottom")}),-1.0]])]});
            extrude(context, id + "F30", {"entities" : qUnion([Q0, Q1, Q2]), "operationType" : NewBodyOperationType.REMOVE, "oppositeDirection" : true, "depth" : 3 * mm});
        }
        {
            var Q0;
            Q0=makeQuery(id+"F1.opExtrude","SWEPT_FACE",FACE,{"disambiguationData":[OSD([sQuery(id+"F0.wireOp",EDGE,"E0.bottom")])]});
            var sketch = newSketch(context, id + "F31", { "sketchPlane" : qUnion([Q0])});
            skLineSegment(sketch, "E57.bottom", {"start": v(-109.66, 0) * mm, "end": v(-89.7, 0) * mm});
            skLineSegment(sketch, "E57.top", {"start": v(-109.66, 3) * mm, "end": v(-89.7, 3) * mm});
            skLineSegment(sketch, "E57.left", {"start": v(-109.66, 0) * mm, "end": v(-109.66, 3) * mm});
            skLineSegment(sketch, "E57.right", {"start": v(-89.7, 0) * mm, "end": v(-89.7, 3) * mm});
            skLineSegment(sketch, "E58.bottom", {"start": v(90.34, 0) * mm, "end": v(110.3, 0) * mm});
            skLineSegment(sketch, "E58.top", {"start": v(90.34, 3) * mm, "end": v(110.3, 3) * mm});
            skLineSegment(sketch, "E58.left", {"start": v(90.34, 0) * mm, "end": v(90.34, 3) * mm});
            skLineSegment(sketch, "E58.right", {"start": v(110.3, 0) * mm, "end": v(110.3, 3) * mm});
            skLineSegment(sketch, "E59.bottom", {"start": v(10.33, 0) * mm, "end": v(-9.65, 0) * mm});
            skLineSegment(sketch, "E59.top", {"start": v(10.33, 3) * mm, "end": v(-9.65, 3) * mm});
            skLineSegment(sketch, "E59.left", {"start": v(10.33, 0) * mm, "end": v(10.33, 3) * mm});
            skLineSegment(sketch, "E59.right", {"start": v(-9.65, 0) * mm, "end": v(-9.65, 3) * mm});
            skSolve(sketch);
        }
        {
            var Q0;
            Q0=makeQuery(id+"F31.imprint","IMPRINT",FACE,{"disambiguationData":[TD([[makeQuery(id+"F31.imprint","IMPRINT",EDGE,{"derivedFrom":sQuery(id+"F31.wireOp",EDGE,"E57.bottom")}),1.0]])]});
            var Q1;
            Q1=makeQuery(id+"F31.imprint","IMPRINT",FACE,{"disambiguationData":[TD([[makeQuery(id+"F31.imprint","IMPRINT",EDGE,{"derivedFrom":sQuery(id+"F31.wireOp",EDGE,"E58.bottom")}),1.0]])]});
            var Q2;
            Q2=makeQuery(id+"F31.imprint","IMPRINT",FACE,{"disambiguationData":[TD([[makeQuery(id+"F31.imprint","IMPRINT",EDGE,{"derivedFrom":sQuery(id+"F31.wireOp",EDGE,"E59.bottom")}),1.0]])]});
            extrude(context, id + "F32", {"entities" : qUnion([Q0, Q1, Q2]), "depth" : 3 * mm});
        }
        {
            var Q0;
            Q0=makeQuery(id+"F1.opExtrude","SWEPT_FACE",FACE,{"disambiguationData":[OSD([sQuery(id+"F0.wireOp",EDGE,"E0.right")])]});
            var sketch = newSketch(context, id + "F33", { "sketchPlane" : qUnion([Q0])});
            skLineSegment(sketch, "E60.bottom", {"start": v(53.76, 0) * mm, "end": v(63.76, 0) * mm});
            skLineSegment(sketch, "E60.top", {"start": v(53.76, 3) * mm, "end": v(63.76, 3) * mm});
            skLineSegment(sketch, "E60.left", {"start": v(53.76, 0) * mm, "end": v(53.76, 3) * mm});
            skLineSegment(sketch, "E60.right", {"start": v(63.76, 0) * mm, "end": v(63.76, 3) * mm});
            skLineSegment(sketch, "E61.bottom", {"start": v(-42.24, 0) * mm, "end": v(-52.22, 0) * mm});
            skLineSegment(sketch, "E61.top", {"start": v(-42.24, 3) * mm, "end": v(-52.22, 3) * mm});
            skLineSegment(sketch, "E61.left", {"start": v(-42.24, 0) * mm, "end": v(-42.24, 3) * mm});
            skLineSegment(sketch, "E61.right", {"start": v(-52.22, 0) * mm, "end": v(-52.22, 3) * mm});
            skSolve(sketch);
        }
        {
            var Q0;
            Q0=makeQuery(id+"F33.imprint","IMPRINT",FACE,{"disambiguationData":[TD([[makeQuery(id+"F33.imprint","IMPRINT",EDGE,{"derivedFrom":sQuery(id+"F33.wireOp",EDGE,"E61.bottom")}),1.0]])]});
            var Q1;
            Q1=makeQuery(id+"F33.imprint","IMPRINT",FACE,{"disambiguationData":[TD([[makeQuery(id+"F33.imprint","IMPRINT",EDGE,{"derivedFrom":sQuery(id+"F33.wireOp",EDGE,"E60.bottom")}),1.0]])]});
            extrude(context, id + "F34", {"entities" : qUnion([Q0, Q1]), "depth" : 3 * mm});
        }
        {
            var Q0;
            Q0=makeQuery(id+"F9.opExtrude","SWEPT_FACE",FACE,{"disambiguationData":[OSD([sQuery(id+"F8.wireOp",EDGE,"E29.right")])]});
            var sketch = newSketch(context, id + "F35", { "sketchPlane" : qUnion([Q0])});
            skLineSegment(sketch, "E62.bottom", {"start": v(-72.24, 50) * mm, "end": v(-69.24, 50) * mm});
            skLineSegment(sketch, "E62.top", {"start": v(-72.24, 40) * mm, "end": v(-69.24, 40) * mm});
            skLineSegment(sketch, "E62.left", {"start": v(-72.24, 50) * mm, "end": v(-72.24, 40) * mm});
            skLineSegment(sketch, "E62.right", {"start": v(-69.24, 50) * mm, "end": v(-69.24, 40) * mm});
            skSolve(sketch);
        }
        {
            var Q0;
            Q0=makeQuery(id+"F35.imprint","IMPRINT",FACE,{"disambiguationData":[TD([[makeQuery(id+"F35.imprint","IMPRINT",EDGE,{"derivedFrom":sQuery(id+"F35.wireOp",EDGE,"E62.bottom")}),-1.0]])]});
            extrude(context, id + "F36", {"entities" : qUnion([Q0]), "depth" : 3 * mm});
        }
        {
            var Q0;
            Q0=makeQuery(id+"F11.opExtrude","SWEPT_FACE",FACE,{"disambiguationData":[OSD([sQuery(id+"F10.wireOp",EDGE,"E32.left")])]});
            var sketch = newSketch(context, id + "F37", { "sketchPlane" : qUnion([Q0])});
            skLineSegment(sketch, "E63.bottom", {"start": v(83.76, 50) * mm, "end": v(80.76, 50) * mm});
            skLineSegment(sketch, "E63.top", {"start": v(83.76, 40) * mm, "end": v(80.76, 40) * mm});
            skLineSegment(sketch, "E63.left", {"start": v(83.76, 50) * mm, "end": v(83.76, 40) * mm});
            skLineSegment(sketch, "E63.right", {"start": v(80.76, 50) * mm, "end": v(80.76, 40) * mm});
            skSolve(sketch);
        }
        {
            var Q0;
            Q0=makeQuery(id+"F37.imprint","IMPRINT",FACE,{"disambiguationData":[TD([[makeQuery(id+"F37.imprint","IMPRINT",EDGE,{"derivedFrom":sQuery(id+"F37.wireOp",EDGE,"E63.bottom")}),1.0]])]});
            extrude(context, id + "F38", {"entities" : qUnion([Q0]), "depth" : 3 * mm});
        }
        {
            var Q0;
            Q0=makeQuery(id+"F1.opExtrude","SWEPT_FACE",FACE,{"disambiguationData":[OSD([sQuery(id+"F0.wireOp",EDGE,"E0.top")])]});
            var sketch = newSketch(context, id + "F39", { "sketchPlane" : qUnion([Q0])});
            skLineSegment(sketch, "E64.bottom", {"start": v(-110.33, 0) * mm, "end": v(-90.35, 0) * mm});
            skLineSegment(sketch, "E64.top", {"start": v(-110.33, 3) * mm, "end": v(-90.35, 3) * mm});
            skLineSegment(sketch, "E64.left", {"start": v(-110.33, 0) * mm, "end": v(-110.33, 3) * mm});
            skLineSegment(sketch, "E64.right", {"start": v(-90.35, 0) * mm, "end": v(-90.35, 3) * mm});
            skLineSegment(sketch, "E65.bottom", {"start": v(-10.33, 0) * mm, "end": v(9.64, 0) * mm});
            skLineSegment(sketch, "E65.top", {"start": v(-10.33, 3) * mm, "end": v(9.64, 3) * mm});
            skLineSegment(sketch, "E65.left", {"start": v(-10.33, 0) * mm, "end": v(-10.33, 3) * mm});
            skLineSegment(sketch, "E65.right", {"start": v(9.64, 0) * mm, "end": v(9.64, 3) * mm});
            skLineSegment(sketch, "E66.bottom", {"start": v(109.65, 0) * mm, "end": v(89.68, 0) * mm});
            skLineSegment(sketch, "E66.top", {"start": v(109.65, 3) * mm, "end": v(89.68, 3) * mm});
            skLineSegment(sketch, "E66.left", {"start": v(109.65, 0) * mm, "end": v(109.65, 3) * mm});
            skLineSegment(sketch, "E66.right", {"start": v(89.68, 0) * mm, "end": v(89.68, 3) * mm});
            skSolve(sketch);
        }
        {
            var Q0;
            Q0=makeQuery(id+"F39.imprint","IMPRINT",FACE,{"disambiguationData":[TD([[makeQuery(id+"F39.imprint","IMPRINT",EDGE,{"derivedFrom":sQuery(id+"F39.wireOp",EDGE,"E66.bottom")}),-1.0]])]});
            var Q1;
            Q1=makeQuery(id+"F39.imprint","IMPRINT",FACE,{"disambiguationData":[TD([[makeQuery(id+"F39.imprint","IMPRINT",EDGE,{"derivedFrom":sQuery(id+"F39.wireOp",EDGE,"E65.bottom")}),-1.0]])]});
            var Q2;
            Q2=makeQuery(id+"F39.imprint","IMPRINT",FACE,{"disambiguationData":[TD([[makeQuery(id+"F39.imprint","IMPRINT",EDGE,{"derivedFrom":sQuery(id+"F39.wireOp",EDGE,"E64.bottom")}),-1.0]])]});
            extrude(context, id + "F40", {"entities" : qUnion([Q0, Q1, Q2]), "depth" : 3 * mm});
        }
        {
            var Q0;
            Q0=makeQuery(id+"F9.opExtrude","SWEPT_FACE",FACE,{"disambiguationData":[OSD([sQuery(id+"F8.wireOp",EDGE,"E30")])]});
            var sketch = newSketch(context, id + "F41", { "sketchPlane" : qUnion([Q0])});
            skLineSegment(sketch, "E67.bottom", {"start": v(-115.1, -72.24) * mm, "end": v(-105.12, -72.24) * mm});
            skLineSegment(sketch, "E67.top", {"start": v(-115.1, -69.24) * mm, "end": v(-105.12, -69.24) * mm});
            skLineSegment(sketch, "E67.left", {"start": v(-115.1, -72.24) * mm, "end": v(-115.1, -69.24) * mm});
            skLineSegment(sketch, "E67.right", {"start": v(-105.12, -72.24) * mm, "end": v(-105.12, -69.24) * mm});
            skLineSegment(sketch, "E68.bottom", {"start": v(58.97, -72.24) * mm, "end": v(68.93, -72.24) * mm});
            skLineSegment(sketch, "E68.top", {"start": v(58.97, -69.24) * mm, "end": v(68.93, -69.24) * mm});
            skLineSegment(sketch, "E68.left", {"start": v(58.97, -72.24) * mm, "end": v(58.97, -69.24) * mm});
            skLineSegment(sketch, "E68.right", {"start": v(68.93, -72.24) * mm, "end": v(68.93, -69.24) * mm});
            skSolve(sketch);
        }
        {
            var Q0;
            Q0=makeQuery(id+"F41.imprint","IMPRINT",FACE,{"disambiguationData":[TD([[makeQuery(id+"F41.imprint","IMPRINT",EDGE,{"derivedFrom":sQuery(id+"F41.wireOp",EDGE,"E67.bottom")}),1.0]])]});
            var Q1;
            Q1=makeQuery(id+"F41.imprint","IMPRINT",FACE,{"disambiguationData":[TD([[makeQuery(id+"F41.imprint","IMPRINT",EDGE,{"derivedFrom":sQuery(id+"F41.wireOp",EDGE,"E68.bottom")}),1.0]])]});
            extrude(context, id + "F42", {"entities" : qUnion([Q0, Q1]), "depth" : 3 * mm});
        }
        {
            var Q0;
            Q0=makeQuery(id+"F11.opExtrude","SWEPT_FACE",FACE,{"disambiguationData":[OSD([sQuery(id+"F10.wireOp",EDGE,"E33")])]});
            var sketch = newSketch(context, id + "F43", { "sketchPlane" : qUnion([Q0])});
            skLineSegment(sketch, "E69.bottom", {"start": v(-105.11, 83.76) * mm, "end": v(-115.1, 83.76) * mm});
            skLineSegment(sketch, "E69.top", {"start": v(-105.11, 80.76) * mm, "end": v(-115.1, 80.76) * mm});
            skLineSegment(sketch, "E69.left", {"start": v(-105.11, 83.76) * mm, "end": v(-105.11, 80.76) * mm});
            skLineSegment(sketch, "E69.right", {"start": v(-115.1, 83.76) * mm, "end": v(-115.1, 80.76) * mm});
            skLineSegment(sketch, "E70.bottom", {"start": v(68.95, 83.76) * mm, "end": v(58.97, 83.76) * mm});
            skLineSegment(sketch, "E70.top", {"start": v(68.95, 80.76) * mm, "end": v(58.97, 80.76) * mm});
            skLineSegment(sketch, "E70.left", {"start": v(68.95, 83.76) * mm, "end": v(68.95, 80.76) * mm});
            skLineSegment(sketch, "E70.right", {"start": v(58.97, 83.76) * mm, "end": v(58.97, 80.76) * mm});
            skSolve(sketch);
        }
        {
            var Q0;
            Q0=makeQuery(id+"F43.imprint","IMPRINT",FACE,{"disambiguationData":[TD([[makeQuery(id+"F43.imprint","IMPRINT",EDGE,{"derivedFrom":sQuery(id+"F43.wireOp",EDGE,"E70.bottom")}),-1.0]])]});
            var Q1;
            Q1=makeQuery(id+"F43.imprint","IMPRINT",FACE,{"disambiguationData":[TD([[makeQuery(id+"F43.imprint","IMPRINT",EDGE,{"derivedFrom":sQuery(id+"F43.wireOp",EDGE,"E69.bottom")}),-1.0]])]});
            extrude(context, id + "F44", {"entities" : qUnion([Q0, Q1]), "depth" : 3 * mm});
        }
    });
